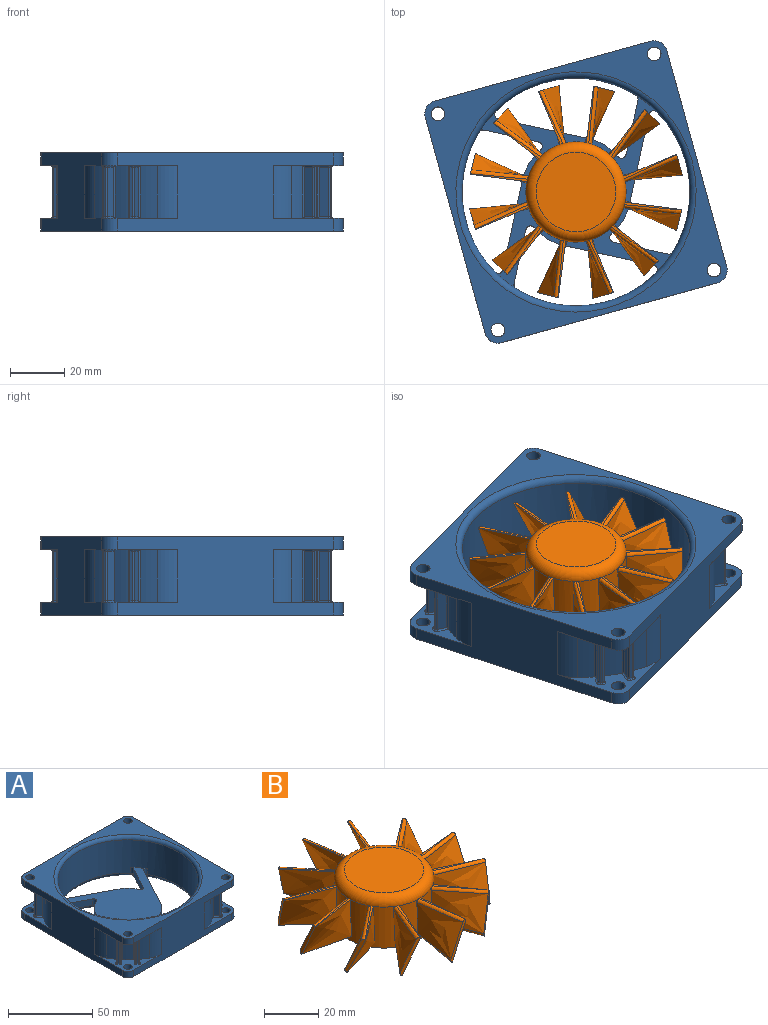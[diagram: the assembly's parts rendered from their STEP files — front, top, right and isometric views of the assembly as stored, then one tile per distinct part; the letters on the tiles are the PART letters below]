
ASSEMBLY  parts=2 mates=1
PART A: 245 faces, bbox 100.9x100.9x33.4 mm
  f0: cylinder r=1.75mm len=4.16mm, axis (0,0,1), area 15.7mm2, adj f1,f15,f32,f44
  f1: plane 73.06x73.06mm, normal (0,0,1), area 1883.8mm2, adj f0,f2,f12,f13,f14,f15,f18,f19
  f2: cylinder r=20.15mm len=9.37mm, axis (0,0,1), area 62mm2, adj f1,f3,f13,f244
  f3: torus R=18.4mm, axis (0,0,-1), area 35.1mm2, adj f2,f4,f5,f243
  f4: torus R=3.51mm, axis (0,0,-1), area 14.6mm2, adj f3,f5,f11,f13
  f5: plane 93.87x93.87mm, normal (0,0,-1), area 2814.2mm2, adj f3,f4,f6,f8,f10,f11,f16,f24
  f6: cylinder r=16.28mm len=32.56mm, axis (0,0,1), area 3mm2, adj f5,f7
  f7: plane 32.56x32.56mm, normal (0,0,-1), area 832.5mm2, adj f6
  f8: torus R=44.11mm, axis (0,0,-1), area 207.1mm2, adj f5,f9,f15,f241
  f9: bspline ~4.7x3.63mm, area 2.6mm2, adj f8,f10,f12,f14
  f10: bspline ~6.51x2.43mm, area 8.6mm2, adj f5,f9,f11
  f11: cylinder r=1.75mm len=18.89mm, axis (-0.47,-0.89,0), area 56.2mm2, adj f4,f5,f10,f12
  f12: plane 18.08x9.51mm, normal (0.89,-0.47,0), area 96mm2, adj f1,f9,f11,f13,f14
  f13: cylinder r=1.75mm len=4.71mm, axis (0,0,1), area 18.4mm2, adj f1,f2,f4,f12
  f14: cylinder r=1.75mm len=4.16mm, axis (0,0,1), area 9mm2, adj f1,f9,f12,f15
  f15: cylinder r=41.81mm len=83.62mm, axis (0,0,1), area 6177.1mm2, adj f0,f1,f8,f14,f16,f18,f30,f31
  f16: torus R=44.11mm, axis (0,0,-1), area 207.1mm2, adj f5,f15,f17,f23
  f17: bspline ~4.7x3.63mm, area 2.6mm2, adj f16,f18,f19,f29
  f18: cylinder r=1.75mm len=4.16mm, axis (0,0,1), area 9mm2, adj f1,f15,f17,f19
  f19: plane 18.08x9.51mm, normal (0.47,0.89,0), area 96mm2, adj f1,f17,f18,f20,f28
  f20: cylinder r=1.75mm len=4.71mm, axis (0,0,1), area 18.4mm2, adj f1,f19,f21,f27
  f21: cylinder r=20.15mm len=9.37mm, axis (0,0,1), area 62mm2, adj f1,f20,f22,f26
  f22: plane 29.73x15.64mm, normal (0.89,-0.47,0), area 157.9mm2, adj f1,f21,f23,f25,f30
  f23: bspline ~5.15x4.64mm, area 7mm2, adj f16,f22,f24,f30
  f24: bspline ~5.41x5.18mm, area 5.4mm2, adj f5,f23,f25
  f25: cylinder r=1.75mm len=30.54mm, axis (-0.47,-0.89,0), area 92.4mm2, adj f5,f22,f24,f26
  f26: torus R=18.4mm, axis (0,0,-1), area 35.1mm2, adj f5,f21,f25,f27
  f27: torus R=3.51mm, axis (0,0,-1), area 14.6mm2, adj f5,f20,f26,f28
  f28: cylinder r=1.75mm len=18.89mm, axis (0.89,-0.47,0), area 56.2mm2, adj f5,f19,f27,f29
  f29: bspline ~6.51x2.43mm, area 8.6mm2, adj f5,f17,f28
  f30: cylinder r=1.75mm len=4.16mm, axis (0,0,1), area 15.7mm2, adj f1,f15,f22,f23
  f31: torus R=44.11mm, axis (0,0,-1), area 207.1mm2, adj f5,f15,f32,f39
  f32: bspline ~5.15x4.64mm, area 7mm2, adj f0,f31,f33,f44
  f33: bspline ~5.41x5.18mm, area 5.4mm2, adj f5,f32,f34
  f34: cylinder r=1.75mm len=30.54mm, axis (0.89,-0.47,0), area 92.4mm2, adj f5,f33,f35,f44
  f35: torus R=18.4mm, axis (0,0,-1), area 35.1mm2, adj f5,f34,f36,f43
  f36: torus R=3.51mm, axis (0,0,-1), area 14.6mm2, adj f5,f35,f37,f42
  f37: cylinder r=1.75mm len=18.89mm, axis (0.47,0.89,0), area 56.2mm2, adj f5,f36,f38,f41
  f38: bspline ~6.51x2.43mm, area 8.6mm2, adj f5,f37,f39
  f39: bspline ~4.7x3.63mm, area 2.6mm2, adj f31,f38,f40,f41
  f40: cylinder r=1.75mm len=4.16mm, axis (0,0,1), area 9mm2, adj f1,f15,f39,f41
  f41: plane 18.08x9.51mm, normal (-0.89,0.47,0), area 96mm2, adj f1,f37,f39,f40,f42
  f42: cylinder r=1.75mm len=4.71mm, axis (0,0,1), area 18.4mm2, adj f1,f36,f41,f43
  f43: cylinder r=20.15mm len=9.37mm, axis (0,0,1), area 62mm2, adj f1,f35,f42,f44
  f44: plane 29.73x15.64mm, normal (0.47,0.89,0), area 157.9mm2, adj f0,f1,f32,f34,f43
  f45: cylinder r=1.75mm len=4.16mm, axis (0,0,1), area 9mm2, adj f1,f15,f46,f49
  f46: bspline ~4.7x3.63mm, area 2.6mm2, adj f45,f47,f49,f59
  f47: bspline ~6.51x2.43mm, area 8.6mm2, adj f5,f46,f48
  f48: cylinder r=1.75mm len=18.89mm, axis (-0.89,0.47,0), area 56.2mm2, adj f5,f47,f49,f58
  f49: plane 18.08x9.51mm, normal (-0.47,-0.89,0), area 96mm2, adj f1,f45,f46,f48,f50
  f50: cylinder r=1.75mm len=4.71mm, axis (0,0,1), area 18.4mm2, adj f1,f49,f51,f58
  f51: cylinder r=20.15mm len=9.37mm, axis (0,0,1), area 62mm2, adj f1,f50,f52,f57
  f52: plane 29.73x15.64mm, normal (-0.89,0.47,0), area 157.9mm2, adj f1,f51,f53,f54,f56
  f53: cylinder r=1.75mm len=4.16mm, axis (0,0,1), area 15.7mm2, adj f1,f15,f52,f54
  f54: bspline ~5.15x4.64mm, area 7mm2, adj f52,f53,f55,f59
  f55: bspline ~5.41x5.18mm, area 5.4mm2, adj f5,f54,f56
  f56: cylinder r=1.75mm len=30.54mm, axis (0.47,0.89,0), area 92.4mm2, adj f5,f52,f55,f57
  f57: torus R=18.4mm, axis (0,0,-1), area 35.1mm2, adj f5,f51,f56,f58
  f58: torus R=3.51mm, axis (0,0,-1), area 14.6mm2, adj f5,f48,f50,f57
  f59: torus R=44.11mm, axis (0,0,-1), area 207.1mm2, adj f5,f15,f46,f54
  f60: torus R=44.11mm, axis (0,0,-1), area 968.1mm2, adj f15,f61
  f61: plane 92x92mm, normal (0,0,1), area 2251.4mm2, adj f60,f62,f85,f86,f92,f110,f111,f121
  f62: plane 82.34x28.75mm, normal (1,0,0), area 1476.4mm2, adj f5,f61,f63,f64,f67,f85,f129,f130
  f63: cylinder r=14.61mm len=19.4mm, axis (0,0,-1), area 148.9mm2, adj f62,f64,f67,f68
  f64: plane 27.8x27.8mm, normal (0,0,1), area 169.3mm2, adj f62,f63,f65,f66,f68,f70,f71,f72
  f65: cylinder r=2.52mm len=5.05mm, axis (0,0,1), area 74.2mm2, adj f5,f64
  f66: cylinder r=50.9mm len=19.4mm, axis (0,0,-1), area 158.8mm2, adj f64,f67,f74,f75,f84,f232
  f67: plane 27.8x27.8mm, normal (0,0,-1), area 169.3mm2, adj f62,f63,f66,f68,f80,f81,f82,f83
  f68: cylinder r=50.9mm len=19.4mm, axis (0,0,-1), area 123.5mm2, adj f63,f64,f67,f69,f70,f80
  f69: cylinder r=0.58mm len=19.4mm, axis (0,0,-1), area 17mm2, adj f68,f70,f79,f80
  f70: cylinder r=0.58mm len=3.66mm, axis (-0.78,-0.63,0), area 3.7mm2, adj f64,f68,f69,f71,f79
  f71: torus R=1.17mm, axis (0,0,-1), area 1.1mm2, adj f64,f70,f72,f78
  f72: cylinder r=0.58mm len=1.16mm, axis (0.63,-0.78,0), area 0.9mm2, adj f64,f71,f73,f77
  f73: torus R=1.17mm, axis (0,0,-1), area 1.1mm2, adj f64,f72,f74,f76
  f74: cylinder r=0.58mm len=3.66mm, axis (0.78,0.63,0), area 3.9mm2, adj f64,f66,f73,f75
  f75: plane 18.23x3.28mm, normal (-0.63,0.78,0), area 77mm2, adj f66,f74,f76,f84
  f76: cylinder r=0.58mm len=18.23mm, axis (0,0,1), area 16.7mm2, adj f73,f75,f77,f83
  f77: plane 18.23x0.79mm, normal (0.78,0.63,0), area 18.6mm2, adj f72,f76,f78,f82
  f78: cylinder r=0.58mm len=18.23mm, axis (0,0,-1), area 16.7mm2, adj f71,f77,f79,f81
  f79: plane 18.23x2.84mm, normal (0.63,-0.78,0), area 66.7mm2, adj f69,f70,f78,f80
  f80: cylinder r=0.58mm len=3.66mm, axis (0.78,0.63,0), area 3.7mm2, adj f67,f68,f69,f79,f81
  f81: torus R=1.17mm, axis (0,0,-1), area 1.1mm2, adj f67,f78,f80,f82
  f82: cylinder r=0.58mm len=1.16mm, axis (-0.63,0.78,0), area 0.9mm2, adj f67,f77,f81,f83
  f83: torus R=1.17mm, axis (0,0,-1), area 1.1mm2, adj f67,f76,f82,f84
  f84: cylinder r=0.58mm len=3.66mm, axis (-0.78,-0.63,0), area 3.9mm2, adj f66,f67,f75,f83
  f85: cylinder r=4.83mm len=4.83mm, axis (0,0,1), area 35.5mm2, adj f61,f62,f67,f86
  f86: plane 82.34x28.75mm, normal (0,1,0), area 1476.4mm2, adj f5,f61,f64,f67,f85,f87,f88,f91
  f87: cylinder r=14.61mm len=19.4mm, axis (0,0,-1), area 148.9mm2, adj f86,f88,f91,f101
  f88: plane 27.8x27.8mm, normal (0,0,1), area 167.2mm2, adj f86,f87,f89,f90,f96,f97,f98,f99
  f89: cylinder r=2.52mm len=5.05mm, axis (0,0,1), area 74.2mm2, adj f5,f88
  f90: cylinder r=50.9mm len=19.4mm, axis (0,0,-1), area 148.1mm2, adj f88,f91,f94,f95,f96,f209,f210,f211
  f91: plane 27.8x27.8mm, normal (0,0,-1), area 167.2mm2, adj f86,f87,f90,f92,f93,f94,f101,f103
  f92: cylinder r=2.52mm len=5.05mm, axis (0,0,1), area 74.2mm2, adj f61,f91
  f93: torus R=1.17mm, axis (0,0,-1), area 1.1mm2, adj f91,f94,f105,f107
  f94: cylinder r=0.58mm len=3.66mm, axis (0.63,-0.78,0), area 3.9mm2, adj f90,f91,f93,f95
  f95: plane 18.23x3.28mm, normal (-0.78,-0.63,0), area 77mm2, adj f90,f94,f96,f107
  f96: cylinder r=0.58mm len=3.66mm, axis (-0.63,0.78,0), area 3.9mm2, adj f88,f90,f95,f97
  f97: torus R=1.17mm, axis (0,0,-1), area 1.1mm2, adj f88,f96,f98,f107
  f98: cylinder r=0.58mm len=1.16mm, axis (0.78,0.63,0), area 0.9mm2, adj f88,f97,f99,f106
  f99: torus R=1.17mm, axis (0,0,-1), area 1.1mm2, adj f88,f98,f100,f108
  f100: cylinder r=0.58mm len=3.66mm, axis (0.63,-0.78,0), area 3.7mm2, adj f88,f99,f101,f102,f109
  f101: cylinder r=50.9mm len=19.4mm, axis (0,0,-1), area 123.5mm2, adj f87,f88,f91,f100,f102,f103
  f102: cylinder r=0.58mm len=19.4mm, axis (0,0,-1), area 16.9mm2, adj f100,f101,f103,f109
  f103: cylinder r=0.58mm len=3.66mm, axis (-0.63,0.78,0), area 3.7mm2, adj f91,f101,f102,f104,f109
  f104: torus R=1.17mm, axis (0,0,-1), area 1.1mm2, adj f91,f103,f105,f108
  f105: cylinder r=0.58mm len=1.16mm, axis (-0.78,-0.63,0), area 0.9mm2, adj f91,f93,f104,f106
  f106: plane 18.23x0.79mm, normal (-0.63,0.78,0), area 18.6mm2, adj f98,f105,f107,f108
  f107: cylinder r=0.58mm len=18.23mm, axis (0,0,1), area 16.7mm2, adj f93,f95,f97,f106
  f108: cylinder r=0.58mm len=18.23mm, axis (0,0,-1), area 16.7mm2, adj f99,f104,f106,f109
  f109: plane 18.23x2.84mm, normal (0.78,0.63,0), area 66.7mm2, adj f100,f102,f103,f108
  f110: cylinder r=4.83mm len=4.83mm, axis (0,0,1), area 35.5mm2, adj f61,f86,f91,f111
  f111: plane 82.34x28.75mm, normal (-1,0,0), area 1476.4mm2, adj f5,f61,f88,f91,f110,f112,f113,f120
  f112: cylinder r=14.61mm len=19.4mm, axis (0,0,-1), area 148.9mm2, adj f111,f113,f120,f191
  f113: plane 27.8x27.8mm, normal (0,0,1), area 167.2mm2, adj f111,f112,f114,f115,f116,f117,f124,f125
  f114: cylinder r=2.52mm len=5.05mm, axis (0,0,1), area 74.2mm2, adj f5,f113
  f115: torus R=1.17mm, axis (0,0,-1), area 1.1mm2, adj f113,f116,f175,f180
  f116: cylinder r=0.58mm len=3.66mm, axis (0.63,0.78,0), area 3.7mm2, adj f113,f115,f117,f118,f181
  f117: cylinder r=50.9mm len=19.4mm, axis (0,0,-1), area 137.2mm2, adj f113,f116,f118,f119,f120,f184,f185,f186
  f118: cylinder r=0.58mm len=19.4mm, axis (0,0,-1), area 17mm2, adj f116,f117,f119,f181
  f119: cylinder r=0.58mm len=3.66mm, axis (-0.63,-0.78,0), area 3.7mm2, adj f117,f118,f120,f181,f182
  f120: plane 27.8x27.8mm, normal (0,0,-1), area 167.2mm2, adj f111,f112,f117,f119,f121,f122,f123,f124
  f121: cylinder r=2.52mm len=5.05mm, axis (0,0,1), area 74.2mm2, adj f61,f120
  f122: torus R=1.17mm, axis (0,0,-1), area 1.1mm2, adj f120,f123,f177,f183
  f123: cylinder r=0.58mm len=3.66mm, axis (0.63,0.78,0), area 3.7mm2, adj f120,f122,f124,f178,f179
  f124: cylinder r=50.9mm len=19.4mm, axis (0,0,-1), area 123.5mm2, adj f113,f120,f123,f125,f173,f179
  f125: cylinder r=14.61mm len=19.4mm, axis (0,0,-1), area 148.9mm2, adj f113,f120,f124,f126
  f126: plane 82.34x28.75mm, normal (0,-1,0), area 1476.4mm2, adj f5,f61,f113,f120,f125,f127,f128,f129
  f127: cylinder r=4.83mm len=4.83mm, axis (0,0,1), area 35.5mm2, adj f5,f111,f113,f126
  f128: cylinder r=4.83mm len=4.83mm, axis (0,0,1), area 35.5mm2, adj f61,f111,f120,f126
  f129: cylinder r=4.83mm len=4.83mm, axis (0,0,1), area 35.5mm2, adj f61,f62,f126,f130
  f130: plane 27.8x27.8mm, normal (0,0,-1), area 167.2mm2, adj f62,f126,f129,f131,f132,f146,f147,f148
  f131: cylinder r=50.9mm len=19.4mm, axis (0,0,-1), area 148.1mm2, adj f130,f132,f133,f134,f142,f160,f161,f170
  f132: cylinder r=0.58mm len=3.66mm, axis (0.78,-0.63,0), area 3.7mm2, adj f130,f131,f133,f151,f171
  f133: cylinder r=0.58mm len=19.4mm, axis (0,0,-1), area 16.9mm2, adj f131,f132,f134,f171
  f134: cylinder r=0.58mm len=3.66mm, axis (-0.78,0.63,0), area 3.7mm2, adj f131,f133,f135,f142,f171
  f135: torus R=1.17mm, axis (0,0,-1), area 1.1mm2, adj f134,f136,f142,f144
  f136: cylinder r=0.58mm len=18.23mm, axis (0,0,1), area 16.7mm2, adj f135,f137,f151,f171
  f137: plane 18.23x0.79mm, normal (0.78,-0.63,0), area 18.6mm2, adj f136,f138,f144,f150
  f138: cylinder r=0.58mm len=18.23mm, axis (0,0,-1), area 16.7mm2, adj f137,f139,f145,f149
  f139: plane 18.23x2.84mm, normal (0.63,0.78,0), area 66.7mm2, adj f138,f140,f141,f148
  f140: cylinder r=0.58mm len=19.4mm, axis (0,0,-1), area 17mm2, adj f139,f141,f146,f148
  f141: cylinder r=0.58mm len=3.66mm, axis (0.78,-0.63,0), area 3.7mm2, adj f139,f140,f142,f145,f146
  f142: plane 27.8x27.8mm, normal (0,0,1), area 167.2mm2, adj f62,f126,f131,f134,f135,f141,f143,f144
  f143: cylinder r=2.52mm len=5.05mm, axis (0,0,1), area 74.2mm2, adj f5,f142
  f144: cylinder r=0.58mm len=1.16mm, axis (-0.63,-0.78,0), area 0.9mm2, adj f135,f137,f142,f145
  f145: torus R=1.17mm, axis (0,0,-1), area 1.1mm2, adj f138,f141,f142,f144
  f146: cylinder r=50.9mm len=19.4mm, axis (0,0,-1), area 123.5mm2, adj f130,f140,f141,f142,f147,f148
  f147: cylinder r=14.61mm len=19.4mm, axis (0,0,-1), area 148.9mm2, adj f62,f130,f142,f146
  f148: cylinder r=0.58mm len=3.66mm, axis (-0.78,0.63,0), area 3.7mm2, adj f130,f139,f140,f146,f149
  f149: torus R=1.17mm, axis (0,0,-1), area 1.1mm2, adj f130,f138,f148,f150
  f150: cylinder r=0.58mm len=1.16mm, axis (0.63,0.78,0), area 0.9mm2, adj f130,f137,f149,f151
  f151: torus R=1.17mm, axis (0,0,-1), area 1.1mm2, adj f130,f132,f136,f150
  f152: cylinder r=4.83mm len=4.83mm, axis (0,0,1), area 35.5mm2, adj f5,f62,f126,f142
  f153: cylinder r=14.61mm len=19.4mm, axis (0,0,-1), area 148.9mm2, adj f126,f130,f142,f154
  f154: cylinder r=50.9mm len=19.4mm, axis (0,0,-1), area 123.5mm2, adj f130,f142,f153,f155,f156,f166
  f155: cylinder r=0.58mm len=19.4mm, axis (0,0,-1), area 16.9mm2, adj f154,f156,f165,f166
  f156: cylinder r=0.58mm len=3.66mm, axis (-0.63,0.78,0), area 3.7mm2, adj f142,f154,f155,f157,f165
  f157: torus R=1.17mm, axis (0,0,-1), area 1.1mm2, adj f142,f156,f158,f164
  f158: cylinder r=0.58mm len=1.16mm, axis (-0.78,-0.63,0), area 0.9mm2, adj f142,f157,f159,f163
  f159: torus R=1.17mm, axis (0,0,-1), area 1.1mm2, adj f142,f158,f160,f162
  f160: cylinder r=0.58mm len=3.66mm, axis (0.63,-0.78,0), area 3.9mm2, adj f131,f142,f159,f161
  f161: plane 18.23x3.28mm, normal (0.78,0.63,0), area 77mm2, adj f131,f160,f162,f170
  f162: cylinder r=0.58mm len=18.23mm, axis (0,0,1), area 16.7mm2, adj f159,f161,f163,f169
  f163: plane 18.23x0.79mm, normal (0.63,-0.78,0), area 18.6mm2, adj f158,f162,f164,f168
  f164: cylinder r=0.58mm len=18.23mm, axis (0,0,-1), area 16.7mm2, adj f157,f163,f165,f167
  f165: plane 18.23x2.84mm, normal (-0.78,-0.63,0), area 66.7mm2, adj f155,f156,f164,f166
  f166: cylinder r=0.58mm len=3.66mm, axis (0.63,-0.78,0), area 3.7mm2, adj f130,f154,f155,f165,f167
  f167: torus R=1.17mm, axis (0,0,-1), area 1.1mm2, adj f130,f164,f166,f168
  f168: cylinder r=0.58mm len=1.16mm, axis (0.78,0.63,0), area 0.9mm2, adj f130,f163,f167,f169
  f169: torus R=1.17mm, axis (0,0,-1), area 1.1mm2, adj f130,f162,f168,f170
  f170: cylinder r=0.58mm len=3.66mm, axis (-0.63,0.78,0), area 3.9mm2, adj f130,f131,f161,f169
  f171: plane 18.23x2.84mm, normal (-0.63,-0.78,0), area 66.7mm2, adj f132,f133,f134,f136
  f172: cylinder r=2.52mm len=5.05mm, axis (0,0,1), area 74.2mm2, adj f61,f130
  f173: cylinder r=0.58mm len=3.66mm, axis (-0.63,-0.78,0), area 3.7mm2, adj f113,f124,f174,f178,f179
  f174: torus R=1.17mm, axis (0,0,-1), area 1.1mm2, adj f113,f173,f175,f177
  f175: cylinder r=0.58mm len=1.16mm, axis (-0.78,0.63,0), area 0.9mm2, adj f113,f115,f174,f176
  f176: plane 18.23x0.79mm, normal (-0.63,-0.78,0), area 18.6mm2, adj f175,f177,f180,f183
  f177: cylinder r=0.58mm len=18.23mm, axis (0,0,-1), area 16.7mm2, adj f122,f174,f176,f178
  f178: plane 18.23x2.84mm, normal (0.78,-0.63,0), area 66.7mm2, adj f123,f173,f177,f179
  f179: cylinder r=0.58mm len=19.4mm, axis (0,0,-1), area 16.9mm2, adj f123,f124,f173,f178
  f180: cylinder r=0.58mm len=18.23mm, axis (0,0,1), area 16.7mm2, adj f115,f176,f181,f182
  f181: plane 18.23x2.84mm, normal (-0.78,0.63,0), area 66.7mm2, adj f116,f118,f119,f180
  f182: torus R=1.17mm, axis (0,0,-1), area 1.1mm2, adj f119,f120,f180,f183
  f183: cylinder r=0.58mm len=1.16mm, axis (0.78,-0.63,0), area 0.9mm2, adj f120,f122,f176,f182
  f184: cylinder r=0.58mm len=3.66mm, axis (0.78,0.63,0), area 3.7mm2, adj f117,f120,f185,f196,f198
  f185: cylinder r=0.58mm len=19.4mm, axis (0,0,-1), area 16.9mm2, adj f117,f184,f186,f198
  f186: cylinder r=0.58mm len=3.66mm, axis (-0.78,-0.63,0), area 3.7mm2, adj f113,f117,f185,f187,f198
  f187: torus R=1.17mm, axis (0,0,-1), area 1.1mm2, adj f113,f186,f188,f197
  f188: cylinder r=0.58mm len=1.16mm, axis (-0.63,0.78,0), area 0.9mm2, adj f113,f187,f189,f199
  f189: torus R=1.17mm, axis (0,0,-1), area 1.1mm2, adj f113,f188,f190,f200
  f190: cylinder r=0.58mm len=3.66mm, axis (0.78,0.63,0), area 3.7mm2, adj f113,f189,f191,f192,f201
  f191: cylinder r=50.9mm len=19.4mm, axis (0,0,-1), area 123.5mm2, adj f112,f113,f120,f190,f192,f193
  f192: cylinder r=0.58mm len=19.4mm, axis (0,0,-1), area 17mm2, adj f190,f191,f193,f201
  f193: cylinder r=0.58mm len=3.66mm, axis (-0.78,-0.63,0), area 3.7mm2, adj f120,f191,f192,f194,f201
  f194: torus R=1.17mm, axis (0,0,-1), area 1.1mm2, adj f120,f193,f195,f200
  f195: cylinder r=0.58mm len=1.16mm, axis (0.63,-0.78,0), area 0.9mm2, adj f120,f194,f196,f199
  f196: torus R=1.17mm, axis (0,0,-1), area 1.1mm2, adj f120,f184,f195,f197
  f197: cylinder r=0.58mm len=18.23mm, axis (0,0,1), area 16.7mm2, adj f187,f196,f198,f199
  f198: plane 18.23x2.84mm, normal (0.63,-0.78,0), area 66.7mm2, adj f184,f185,f186,f197
  f199: plane 18.23x0.79mm, normal (-0.78,-0.63,0), area 18.6mm2, adj f188,f195,f197,f200
  f200: cylinder r=0.58mm len=18.23mm, axis (0,0,-1), area 16.7mm2, adj f189,f194,f199,f201
  f201: plane 18.23x2.84mm, normal (-0.63,0.78,0), area 66.7mm2, adj f190,f192,f193,f200
  f202: cylinder r=4.83mm len=4.83mm, axis (0,0,1), area 35.5mm2, adj f5,f86,f88,f111
  f203: cylinder r=14.61mm len=19.4mm, axis (0,0,-1), area 148.9mm2, adj f88,f91,f111,f204
  f204: cylinder r=50.9mm len=19.4mm, axis (0,0,-1), area 123.5mm2, adj f88,f91,f203,f205,f215,f216
  f205: cylinder r=0.58mm len=3.66mm, axis (-0.78,0.63,0), area 3.7mm2, adj f88,f204,f206,f216,f217
  f206: torus R=1.17mm, axis (0,0,-1), area 1.1mm2, adj f88,f205,f207,f218
  f207: cylinder r=0.58mm len=1.16mm, axis (0.63,0.78,0), area 0.9mm2, adj f88,f206,f208,f219
  f208: torus R=1.17mm, axis (0,0,-1), area 1.1mm2, adj f88,f207,f209,f220
  f209: cylinder r=0.58mm len=3.66mm, axis (0.78,-0.63,0), area 3.7mm2, adj f88,f90,f208,f210,f221
  f210: cylinder r=0.58mm len=19.4mm, axis (0,0,-1), area 16.9mm2, adj f90,f209,f211,f221
  f211: cylinder r=0.58mm len=3.66mm, axis (-0.78,0.63,0), area 3.7mm2, adj f90,f91,f210,f212,f221
  f212: torus R=1.17mm, axis (0,0,-1), area 1.1mm2, adj f91,f211,f213,f220
  f213: cylinder r=0.58mm len=1.16mm, axis (-0.63,-0.78,0), area 0.9mm2, adj f91,f212,f214,f219
  f214: torus R=1.17mm, axis (0,0,-1), area 1.1mm2, adj f91,f213,f215,f218
  f215: cylinder r=0.58mm len=3.66mm, axis (0.78,-0.63,0), area 3.7mm2, adj f91,f204,f214,f216,f217
  f216: cylinder r=0.58mm len=19.4mm, axis (0,0,-1), area 17mm2, adj f204,f205,f215,f217
  f217: plane 18.23x2.84mm, normal (-0.63,-0.78,0), area 66.7mm2, adj f205,f215,f216,f218
  f218: cylinder r=0.58mm len=18.23mm, axis (0,0,-1), area 16.7mm2, adj f206,f214,f217,f219
  f219: plane 18.23x0.79mm, normal (-0.78,0.63,0), area 18.6mm2, adj f207,f213,f218,f220
  f220: cylinder r=0.58mm len=18.23mm, axis (0,0,1), area 16.7mm2, adj f208,f212,f219,f221
  f221: plane 18.23x2.84mm, normal (0.63,0.78,0), area 66.7mm2, adj f209,f210,f211,f220
  f222: cylinder r=4.83mm len=4.83mm, axis (0,0,1), area 35.5mm2, adj f5,f62,f64,f86
  f223: cylinder r=14.61mm len=19.4mm, axis (0,0,-1), area 148.9mm2, adj f64,f67,f86,f224
  f224: cylinder r=50.9mm len=19.4mm, axis (0,0,-1), area 123.5mm2, adj f64,f67,f223,f225,f226,f237
  f225: cylinder r=0.58mm len=19.4mm, axis (0,0,-1), area 16.9mm2, adj f224,f226,f237,f238
  f226: cylinder r=0.58mm len=3.66mm, axis (0.63,0.78,0), area 3.7mm2, adj f67,f224,f225,f227,f238
  f227: torus R=1.17mm, axis (0,0,-1), area 1.1mm2, adj f67,f226,f228,f235
  f228: cylinder r=0.58mm len=18.23mm, axis (0,0,-1), area 16.7mm2, adj f227,f229,f236,f238
  f229: torus R=1.17mm, axis (0,0,-1), area 1.1mm2, adj f64,f228,f230,f237
  f230: cylinder r=0.58mm len=1.16mm, axis (-0.78,0.63,0), area 0.9mm2, adj f64,f229,f231,f236
  f231: torus R=1.17mm, axis (0,0,-1), area 1.6mm2, adj f64,f230,f232,f233
  f232: plane 19.87x3.75mm, normal (0.78,-0.63,0), area 81.5mm2, adj f64,f66,f67,f231,f233,f234
  f233: cylinder r=0.58mm len=18.23mm, axis (0,0,1), area 16.7mm2, adj f231,f232,f234,f236
  f234: torus R=1.17mm, axis (0,0,-1), area 1.6mm2, adj f67,f232,f233,f235
  f235: cylinder r=0.58mm len=1.16mm, axis (0.78,-0.63,0), area 0.9mm2, adj f67,f227,f234,f236
  f236: plane 18.23x0.79mm, normal (0.63,0.78,0), area 18.6mm2, adj f228,f230,f233,f235
  f237: cylinder r=0.58mm len=3.66mm, axis (0.63,0.78,0), area 3.7mm2, adj f64,f224,f225,f229,f238
  f238: plane 18.23x2.84mm, normal (-0.78,0.63,0), area 66.7mm2, adj f225,f226,f228,f237
  f239: cylinder r=2.52mm len=5.05mm, axis (0,0,1), area 74.2mm2, adj f61,f67
  f240: cylinder r=1.75mm len=4.16mm, axis (0,0,1), area 15.7mm2, adj f1,f15,f241,f244
  f241: bspline ~5.15x4.64mm, area 7mm2, adj f8,f240,f242,f244
  f242: bspline ~5.41x5.18mm, area 5.4mm2, adj f5,f241,f243
  f243: cylinder r=1.75mm len=30.54mm, axis (-0.89,0.47,0), area 92.4mm2, adj f3,f5,f242,f244
  f244: plane 29.73x15.64mm, normal (-0.47,-0.89,0), area 157.9mm2, adj f1,f2,f240,f241,f243
PART B: 88 faces, bbox 79.5x79.5x22.4 mm
  f0: plane 16.12x6.98mm, normal (-0.5,-0.87,0), area 23mm2, adj f1,f8,f9,f10,f11,f12
  f1: bspline ~20.45x14.9mm, area 300.9mm2, adj f0,f2,f10,f12
  f2: cylinder r=18.4mm len=36.8mm, axis (0,0,1), area 1728.8mm2, adj f1,f3,f4,f5,f6,f7,f8,f9
  f3: plane 36.8x36.8mm, normal (0,0,-1), area 1063.6mm2, adj f2
  f4: bspline ~21.62x5.22mm, area 38.3mm2, adj f2,f5,f27,f28
  f5: bspline ~21.73x14.9mm, area 300.9mm2, adj f2,f4,f6,f28
  f6: bspline ~21.63x4.68mm, area 37.1mm2, adj f2,f5,f7,f25,f28
  f7: torus R=14.61mm, axis (0,0,-1), area 637.1mm2, adj f2,f6,f8,f11,f12,f13,f17,f18
  f8: bspline ~20.28x17.09mm, area 348.8mm2, adj f0,f2,f7,f9,f11
  f9: bspline ~16.81x15.89mm, area 11mm2, adj f0,f2,f8,f10
  f10: bspline ~17.22x15.13mm, area 38.4mm2, adj f0,f1,f2,f9
  f11: bspline ~20.71x9.06mm, area 12.2mm2, adj f0,f7,f8,f12
  f12: bspline ~20.77x9.16mm, area 37.1mm2, adj f0,f1,f2,f7,f11
  f13: bspline ~21.47x17.09mm, area 348.8mm2, adj f2,f7,f14,f15,f18
  f14: bspline ~21.73x7.38mm, area 11mm2, adj f2,f13,f15,f19
  f15: plane 16.12x6.98mm, normal (-0.87,-0.5,0), area 23mm2, adj f13,f14,f16,f17,f18,f19
  f16: bspline ~20.74x14.9mm, area 300.9mm2, adj f2,f15,f17,f19
  f17: bspline ~17.78x14.69mm, area 37.1mm2, adj f2,f7,f15,f16,f18
  f18: bspline ~17.77x14.15mm, area 12.2mm2, adj f7,f13,f15,f17
  f19: bspline ~20.99x8.2mm, area 38.4mm2, adj f2,f14,f15,f16
  f20: bspline ~21.74x16.98mm, area 348.8mm2, adj f2,f7,f21,f22,f30
  f21: bspline ~21.74x5.79mm, area 11mm2, adj f2,f20,f22,f66
  f22: plane 16.12x8.04mm, normal (-1,0,0), area 23mm2, adj f20,f21,f23,f24,f30,f66
  f23: bspline ~21.73x14.9mm, area 300.9mm2, adj f2,f22,f24,f66
  f24: bspline ~21.64x4.68mm, area 37.1mm2, adj f2,f7,f22,f23,f30
  f25: bspline ~21.71x3.81mm, area 12.2mm2, adj f6,f7,f26,f28
  f26: bspline ~21.74x17.09mm, area 348.8mm2, adj f2,f7,f25,f27,f28
  f27: bspline ~21.74x5.79mm, area 11mm2, adj f2,f4,f26,f28
  f28: plane 16.12x8.04mm, normal (1,0,0), area 23mm2, adj f4,f5,f6,f25,f26,f27
  f29: plane 29.21x29.21mm, normal (0,0,1), area 670.1mm2, adj f7
  f30: bspline ~21.71x3.81mm, area 12.2mm2, adj f7,f20,f22,f24
  f31: bspline ~20.28x17.09mm, area 348.8mm2, adj f2,f7,f32,f33,f36
  f32: bspline ~16.81x15.89mm, area 11mm2, adj f2,f31,f33,f37
  f33: plane 16.12x6.98mm, normal (-0.87,0.5,0), area 23mm2, adj f31,f32,f34,f35,f36,f37
  f34: bspline ~20.45x14.9mm, area 300.9mm2, adj f2,f33,f35,f37
  f35: bspline ~20.77x9.16mm, area 37.1mm2, adj f2,f7,f33,f34,f36
  f36: bspline ~20.71x9.06mm, area 12.2mm2, adj f7,f31,f33,f35
  f37: bspline ~17.22x15.13mm, area 38.4mm2, adj f2,f32,f33,f34
  f38: bspline ~21.47x17.09mm, area 348.8mm2, adj f2,f7,f39,f40,f43
  f39: bspline ~21.73x7.38mm, area 11mm2, adj f2,f38,f40,f44
  f40: plane 16.12x6.98mm, normal (-0.5,0.87,0), area 23mm2, adj f38,f39,f41,f42,f43,f44
  f41: bspline ~20.74x14.9mm, area 300.9mm2, adj f2,f40,f42,f44
  f42: bspline ~17.78x14.69mm, area 37.1mm2, adj f2,f7,f40,f41,f43
  f43: bspline ~17.77x14.15mm, area 12.2mm2, adj f7,f38,f40,f42
  f44: bspline ~20.99x8.2mm, area 38.4mm2, adj f2,f39,f40,f41
  f45: bspline ~21.74x17.09mm, area 348.8mm2, adj f2,f7,f46,f47,f50
  f46: bspline ~21.74x5.79mm, area 11mm2, adj f2,f45,f47,f51
  f47: plane 16.12x8.04mm, normal (0,1,0), area 23mm2, adj f45,f46,f48,f49,f50,f51
  f48: bspline ~21.73x14.9mm, area 300.9mm2, adj f2,f47,f49,f51
  f49: bspline ~21.63x4.68mm, area 37.1mm2, adj f2,f7,f47,f48,f50
  f50: bspline ~21.71x3.81mm, area 12.2mm2, adj f7,f45,f47,f49
  f51: bspline ~21.62x5.22mm, area 38.4mm2, adj f2,f46,f47,f48
  f52: bspline ~20.28x17.09mm, area 348.8mm2, adj f2,f7,f53,f54,f57
  f53: bspline ~16.81x15.89mm, area 11mm2, adj f2,f52,f54,f58
  f54: plane 16.12x6.98mm, normal (0.5,0.87,0), area 23mm2, adj f52,f53,f55,f56,f57,f58
  f55: bspline ~20.45x14.9mm, area 300.9mm2, adj f2,f54,f56,f58
  f56: bspline ~20.77x9.16mm, area 37.1mm2, adj f2,f7,f54,f55,f57
  f57: bspline ~20.71x9.06mm, area 12.2mm2, adj f7,f52,f54,f56
  f58: bspline ~17.22x15.13mm, area 38.4mm2, adj f2,f53,f54,f55
  f59: bspline ~21.44x16.98mm, area 348.8mm2, adj f2,f7,f60,f61,f64
  f60: bspline ~21.73x7.38mm, area 11mm2, adj f2,f59,f61,f65
  f61: plane 16.12x6.98mm, normal (0.87,0.5,0), area 23mm2, adj f59,f60,f62,f63,f64,f65
  f62: bspline ~20.74x14.9mm, area 300.9mm2, adj f2,f61,f63,f65
  f63: bspline ~17.78x14.69mm, area 37.1mm2, adj f2,f7,f61,f62,f64
  f64: bspline ~17.77x14.15mm, area 12.2mm2, adj f7,f59,f61,f63
  f65: bspline ~20.99x8.2mm, area 38.4mm2, adj f2,f60,f61,f62
  f66: bspline ~21.62x5.22mm, area 38.3mm2, adj f2,f21,f22,f23
  f67: bspline ~20.28x17.09mm, area 348.8mm2, adj f2,f7,f68,f69,f72
  f68: bspline ~16.81x15.89mm, area 11mm2, adj f2,f67,f69,f73
  f69: plane 16.12x6.98mm, normal (0.87,-0.5,0), area 23mm2, adj f67,f68,f70,f71,f72,f73
  f70: bspline ~20.45x14.9mm, area 300.9mm2, adj f2,f69,f71,f73
  f71: bspline ~20.77x9.16mm, area 37.1mm2, adj f2,f7,f69,f70,f72
  f72: bspline ~20.71x9.06mm, area 12.2mm2, adj f7,f67,f69,f71
  f73: bspline ~17.22x15.13mm, area 38.4mm2, adj f2,f68,f69,f70
  f74: bspline ~21.44x16.98mm, area 348.8mm2, adj f2,f7,f75,f76,f79
  f75: bspline ~21.73x7.38mm, area 11mm2, adj f2,f74,f76,f80
  f76: plane 16.12x6.98mm, normal (0.5,-0.87,0), area 23mm2, adj f74,f75,f77,f78,f79,f80
  f77: bspline ~20.74x14.9mm, area 300.9mm2, adj f2,f76,f78,f80
  f78: bspline ~17.78x14.69mm, area 37.1mm2, adj f2,f7,f76,f77,f79
  f79: bspline ~17.77x14.15mm, area 12.2mm2, adj f7,f74,f76,f78
  f80: bspline ~20.99x8.2mm, area 38.4mm2, adj f2,f75,f76,f77
  f81: bspline ~21.74x17.09mm, area 348.8mm2, adj f2,f7,f82,f83,f86
  f82: bspline ~21.74x5.79mm, area 11mm2, adj f2,f81,f83,f87
  f83: plane 16.12x8.04mm, normal (0,-1,0), area 23mm2, adj f81,f82,f84,f85,f86,f87
  f84: bspline ~21.73x14.9mm, area 300.9mm2, adj f2,f83,f85,f87
  f85: bspline ~21.64x4.68mm, area 37.1mm2, adj f2,f7,f83,f84,f86
  f86: bspline ~21.71x3.81mm, area 12.2mm2, adj f7,f81,f83,f85
  f87: bspline ~21.62x5.22mm, area 38.4mm2, adj f2,f82,f83,f84
PLACE A rot(axis=(0,0,1),15.5deg) t=(-40.29,11.03,8.4)mm
PLACE B rot(axis=(0,0,1),15.5deg) t=(-45.16,14.11,11.66)mm
MATE fastened A.f2 <-> B.f2  axis (0,0,1) through (-47.51,14.6,14.87)mm
